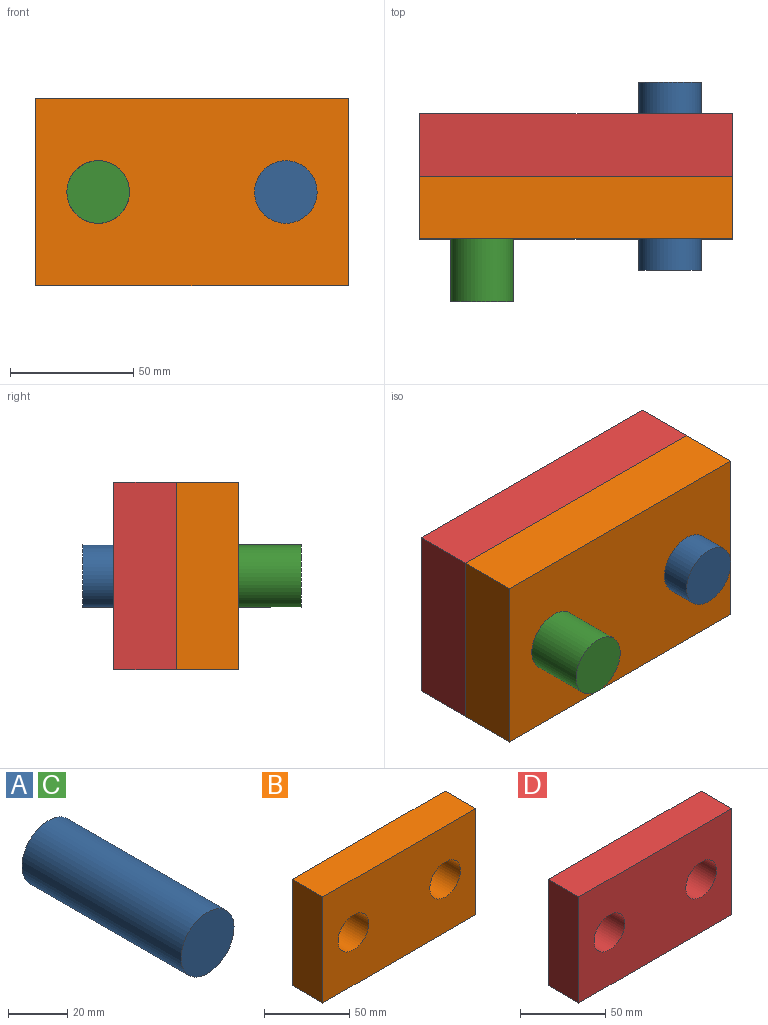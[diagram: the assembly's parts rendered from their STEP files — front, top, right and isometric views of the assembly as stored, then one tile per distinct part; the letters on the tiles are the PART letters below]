
ASSEMBLY  parts=4 mates=4
PART A: 3 faces, bbox 25.4x76.2x25.4 mm
  f0: cylinder r=12.7mm len=76.2mm, axis (0,1,0), area 6080.5mm2, adj f1,f2
  f1: plane 25.4x25.4mm, normal (0,-1,0), area 506.7mm2, adj f0
  f2: plane 25.4x25.4mm, normal (0,1,0), area 506.7mm2, adj f0
PART B: 8 faces, bbox 127x25.4x76.2 mm
  f0: plane 76.2x25.4mm, normal (-1,0,0), area 1935.5mm2, adj f1,f4,f6,f7
  f1: plane 127x25.4mm, normal (0,0,-1), area 3225.8mm2, adj f0,f2,f6,f7
  f2: plane 76.2x25.4mm, normal (1,0,0), area 1935.5mm2, adj f1,f4,f6,f7
  f3: cylinder r=12.7mm len=25.4mm, axis (0,1,0), area 2026.8mm2, adj f6,f7
  f4: plane 127x25.4mm, normal (0,0,1), area 3225.8mm2, adj f0,f2,f6,f7
  f5: cylinder r=12.7mm len=25.4mm, axis (0,1,0), area 2026.8mm2, adj f6,f7
  f6: plane 127x76.2mm, normal (0,-1,0), area 8664mm2, adj f0,f1,f2,f3,f4,f5
  f7: plane 127x76.2mm, normal (0,1,0), area 8664mm2, adj f0,f1,f2,f3,f4,f5
PART C: same geometry as A
PART D: 8 faces, bbox 127x25.4x76.2 mm
  f0: plane 76.2x25.4mm, normal (-1,0,0), area 1935.5mm2, adj f1,f4,f6,f7
  f1: plane 127x25.4mm, normal (0,0,1), area 3225.8mm2, adj f0,f2,f6,f7
  f2: plane 76.2x25.4mm, normal (1,0,0), area 1935.5mm2, adj f1,f4,f6,f7
  f3: cylinder r=12.7mm len=25.4mm, axis (0,-1,0), area 2026.8mm2, adj f6,f7
  f4: plane 127x25.4mm, normal (0,0,-1), area 3225.8mm2, adj f0,f2,f6,f7
  f5: cylinder r=12.7mm len=25.4mm, axis (0,-1,0), area 2026.8mm2, adj f6,f7
  f6: plane 127x76.2mm, normal (0,1,0), area 8664mm2, adj f0,f1,f2,f3,f4,f5
  f7: plane 127x76.2mm, normal (0,-1,0), area 8664mm2, adj f0,f1,f2,f3,f4,f5
PLACE A t=(76.2,-25.4,0)mm
PLACE B t=(0,-25.4,0)mm
PLACE C rot(axis=(1,0,0),180deg) t=(0,-38.1,76.2)mm
PLACE D rot(axis=(1,0,0),180deg) t=(0,0,76.2)mm fixed
MATE cylindrical B.f5 <-> A.f0  axis (0,-1,0) through (101.6,-50.8,38.1)mm
MATE fastened C.f0 <-> D.f3  axis (0,1,0) through (25.4,0,38.1)mm
MATE revolute D.f3 <-> B.f3  axis (0,-1,0) through (25.4,-25.4,38.1)mm
MATE fastened A.f0 <-> D.f5  axis (0,1,0) through (101.6,12.7,38.1)mm
